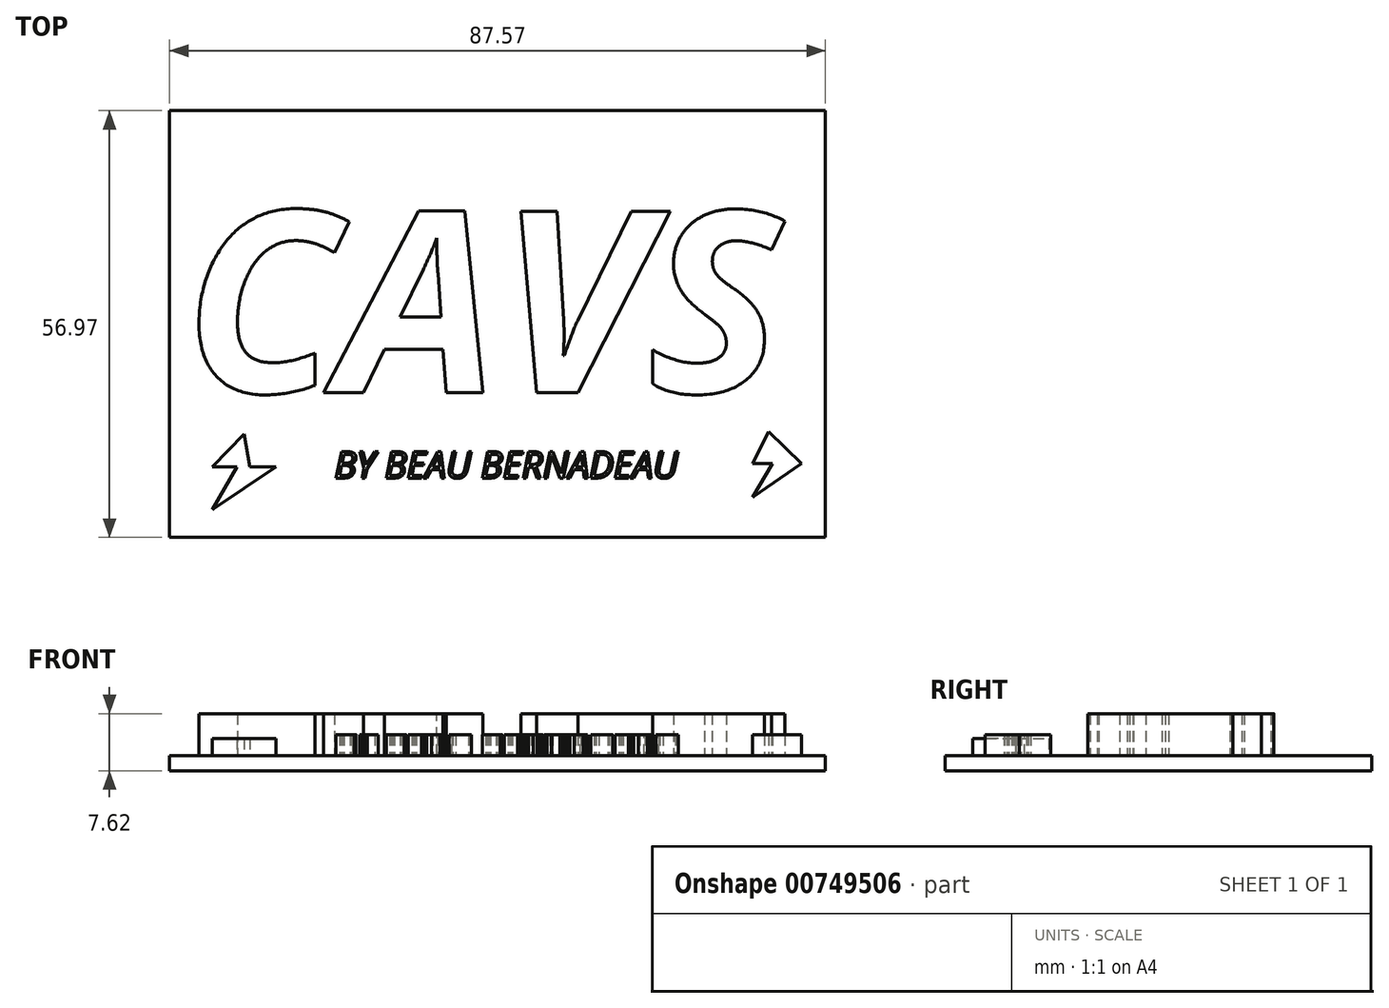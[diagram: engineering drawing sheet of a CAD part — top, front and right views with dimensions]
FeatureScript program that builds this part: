
annotation { "Feature Type Name" : "Feature", "Feature Type Description" : "" }
export const myFeature = defineFeature(function(context is Context, id is Id, definition is map)
    precondition{}
    {
        {
            var Q0;
            Q0=qCreatedBy(makeId("Top.planeOp"),FACE);
            var sketch = newSketch(context, id + "F0", { "sketchPlane" : qUnion([Q0])});
            skLineSegment(sketch, "E0", {"start": v(-47.1, -34.2) * mm, "end": v(40.47, -34.2) * mm});
            skLineSegment(sketch, "E1", {"start": v(40.47, -34.2) * mm, "end": v(40.47, 22.77) * mm});
            skLineSegment(sketch, "E2", {"start": v(40.47, 22.77) * mm, "end": v(-47.1, 22.77) * mm});
            skLineSegment(sketch, "E3", {"start": v(-47.1, 22.77) * mm, "end": v(-47.1, -34.2) * mm});
            skSolve(sketch);
        }
        {
            var Q0;
            Q0 = qSketchRegion(id + "F0", true);
            extrude(context, id + "F1", {"entities" : qUnion([Q0]), "depth" : 2.03 * mm, "offsetDistance" : 25.4 * mm});
        }
        {
            var Q0;
            Q0=makeQuery(id+"F1.opExtrude","CAP_FACE",FACE,{"disambiguationData":[OSD([sQuery(id+"F0.wireOp",EDGE,"E0"),sQuery(id+"F0.wireOp",EDGE,"E1"),sQuery(id+"F0.wireOp",EDGE,"E2"),sQuery(id+"F0.wireOp",EDGE,"E3")])],"isStart":false});
            var sketch = newSketch(context, id + "F2", { "sketchPlane" : qUnion([Q0])});
            skText(sketch, "E4", { "text": "CAVS", "fontName": "OpenSans-BoldItalic.ttf"});
            const initialGuessF2  = {"E4": [-0.04519, -0.01484, 1, 0, 0.02436]};
            skSetInitialGuess(sketch, initialGuessF2);
            skSolve(sketch);
        }
        {
            var Q0;
            Q0 = qSketchRegion(id + "F2", true);
            extrude(context, id + "F3", {"entities" : qUnion([Q0]), "operationType" : NewBodyOperationType.ADD, "depth" : 5.6 * mm, "offsetDistance" : 25.4 * mm});
        }
        {
            var Q0;
            {var subQ0=sQuery(id+"F0.wireOp",EDGE,"E2");var subQ1=sQuery(id+"F0.wireOp",EDGE,"E0");var subQ2=sQuery(id+"F0.wireOp",EDGE,"E3");var subQ3=sQuery(id+"F0.wireOp",EDGE,"E1");Q0=makeQuery(id+"F3.boolean.opBoolean","SPLIT",FACE,{"disambiguationData":[TD([makeQuery(id+"F1.opExtrude","SWEPT_FACE",FACE,{"disambiguationData":[OSD([subQ1])]})])],"derivedFrom":makeQuery(id+"F1.opExtrude","CAP_FACE",FACE,{"disambiguationData":[OSD([subQ1,subQ3,subQ0,subQ2])],"isStart":false})});}
            var sketch = newSketch(context, id + "F4", { "sketchPlane" : qUnion([Q0])});
            skText(sketch, "E5", { "text": "BY BEAU BERNADEAU", "fontName": "OpenSans-Italic.ttf"});
            const initialGuessF4  = {"E5": [-0.02509, -0.02627, 1, 0, 0.00355]};
            skSetInitialGuess(sketch, initialGuessF4);
            skSolve(sketch);
        }
        {
            var Q0;
            Q0 = qSketchRegion(id + "F4", true);
            extrude(context, id + "F5", {"entities" : qUnion([Q0]), "operationType" : NewBodyOperationType.ADD, "depth" : 2.8 * mm, "offsetDistance" : 25.4 * mm});
        }
        {
            var Q0;
            {var subQ38=sQuery(id+"F0.wireOp",EDGE,"E2");var subQ40=sQuery(id+"F0.wireOp",EDGE,"E0");var subQ41=makeQuery(id+"F1.opExtrude","SWEPT_FACE",FACE,{"disambiguationData":[OSD([subQ40])]});var subQ44=sQuery(id+"F0.wireOp",EDGE,"E3");var subQ47=sQuery(id+"F0.wireOp",EDGE,"E1");Q0=makeQuery(id+"F5.boolean.opBoolean","SPLIT",FACE,{"disambiguationData":[TD([subQ41])],"derivedFrom":makeQuery(id+"F3.boolean.opBoolean","SPLIT",FACE,{"disambiguationData":[TD([subQ41])],"derivedFrom":makeQuery(id+"F1.opExtrude","CAP_FACE",FACE,{"disambiguationData":[OSD([subQ40,subQ47,subQ38,subQ44])],"isStart":false})})});}
            var sketch = newSketch(context, id + "F6", { "sketchPlane" : qUnion([Q0])});
            skLineSegment(sketch, "E6", {"start": v(-37.15, -20.37) * mm, "end": v(-41.39, -24.8) * mm});
            skLineSegment(sketch, "E7", {"start": v(-41.39, -24.8) * mm, "end": v(-38.07, -24.8) * mm});
            skLineSegment(sketch, "E8", {"start": v(-38.07, -24.8) * mm, "end": v(-41.39, -30.51) * mm});
            skLineSegment(sketch, "E9", {"start": v(-41.39, -30.51) * mm, "end": v(-32.9, -24.8) * mm});
            skLineSegment(sketch, "E10", {"start": v(-32.9, -24.8) * mm, "end": v(-36.41, -24.8) * mm});
            skLineSegment(sketch, "E11", {"start": v(-36.41, -24.8) * mm, "end": v(-37.15, -20.37) * mm});
            skSolve(sketch);
        }
        {
            var Q0;
            Q0 = qSketchRegion(id + "F6", true);
            extrude(context, id + "F7", {"entities" : qUnion([Q0]), "operationType" : NewBodyOperationType.ADD, "depth" : 2.3 * mm, "offsetDistance" : 25.4 * mm});
        }
        {
            var Q0;
            {var subQ38=sQuery(id+"F0.wireOp",EDGE,"E2");var subQ40=sQuery(id+"F0.wireOp",EDGE,"E0");var subQ41=makeQuery(id+"F1.opExtrude","SWEPT_FACE",FACE,{"disambiguationData":[OSD([subQ40])]});var subQ44=sQuery(id+"F0.wireOp",EDGE,"E3");var subQ47=sQuery(id+"F0.wireOp",EDGE,"E1");Q0=makeQuery(id+"F5.boolean.opBoolean","SPLIT",FACE,{"disambiguationData":[TD([subQ41])],"derivedFrom":makeQuery(id+"F3.boolean.opBoolean","SPLIT",FACE,{"disambiguationData":[TD([subQ41])],"derivedFrom":makeQuery(id+"F1.opExtrude","CAP_FACE",FACE,{"disambiguationData":[OSD([subQ40,subQ47,subQ38,subQ44])],"isStart":false})})});}
            var sketch = newSketch(context, id + "F8", { "sketchPlane" : qUnion([Q0])});
            skLineSegment(sketch, "E12", {"start": v(32.9, -20.1) * mm, "end": v(30.74, -24.33) * mm});
            skLineSegment(sketch, "E13", {"start": v(30.74, -24.33) * mm, "end": v(33.4, -24.33) * mm});
            skLineSegment(sketch, "E14", {"start": v(33.4, -24.33) * mm, "end": v(30.74, -28.86) * mm});
            skLineSegment(sketch, "E15", {"start": v(30.74, -28.86) * mm, "end": v(37.31, -24.33) * mm});
            skLineSegment(sketch, "E16", {"start": v(37.31, -24.33) * mm, "end": v(32.9, -20.1) * mm});
            skSolve(sketch);
        }
        {
            var Q0;
            Q0 = qSketchRegion(id + "F8", true);
            extrude(context, id + "F9", {"entities" : qUnion([Q0]), "operationType" : NewBodyOperationType.ADD, "depth" : 2.8 * mm, "offsetDistance" : 25.4 * mm});
        }
    });
